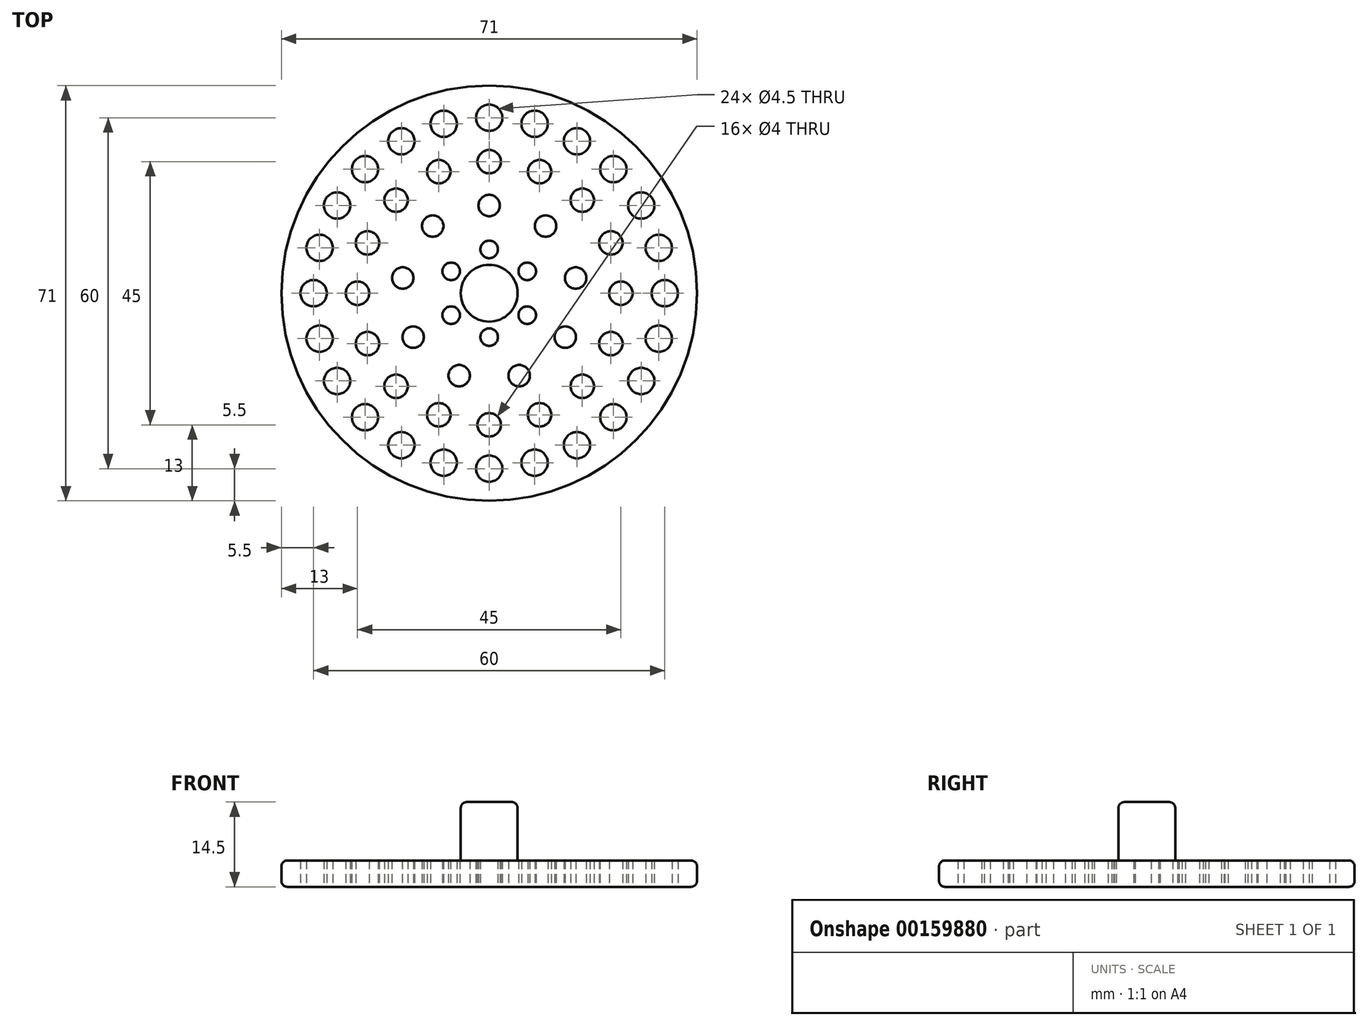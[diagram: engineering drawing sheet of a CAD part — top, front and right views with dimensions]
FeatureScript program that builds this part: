
annotation { "Feature Type Name" : "Feature", "Feature Type Description" : "" }
export const myFeature = defineFeature(function(context is Context, id is Id, definition is map)
    precondition{}
    {
        {
            var Q0;
            Q0=qCreatedBy(makeId("Top.planeOp"),FACE);
            var sketch = newSketch(context, id + "F0", { "sketchPlane" : qUnion([Q0])});
            skCircle(sketch, "E0", {"center": v(0, 0) * mm, "radius": 35.5 * mm});
            skSolve(sketch);
        }
        {
            var Q0;
            Q0=makeQuery(id+"F0.imprint","IMPRINT",FACE,{"disambiguationData":[TD([[makeQuery(id+"F0.imprint","IMPRINT",EDGE,{"derivedFrom":sQuery(id+"F0.wireOp",EDGE,"E0")}),1.0]])]});
            var sketch = newSketch(context, id + "F1", { "sketchPlane" : qUnion([Q0])});
            skCircle(sketch, "E1", {"center": v(0, 0) * mm, "radius": 7.5 * mm, "construction": true});
            skCircle(sketch, "E2", {"center": v(0, 7.5) * mm, "radius": 1.5 * mm});
            skCircle(sketch, "E3.1.1", {"center": v(-6.5, 3.75) * mm, "radius": 1.5 * mm});
            skCircle(sketch, "E3.2.1", {"center": v(-6.5, -3.75) * mm, "radius": 1.5 * mm});
            skCircle(sketch, "E3.3.1", {"center": v(0, -7.5) * mm, "radius": 1.5 * mm});
            skCircle(sketch, "E3.4.1", {"center": v(6.5, -3.75) * mm, "radius": 1.5 * mm});
            skCircle(sketch, "E3.5.1", {"center": v(6.5, 3.75) * mm, "radius": 1.5 * mm});
            skSolve(sketch);
        }
        {
            var Q0;
            Q0=makeQuery(id+"F0.imprint","IMPRINT",FACE,{"disambiguationData":[TD([[makeQuery(id+"F0.imprint","IMPRINT",EDGE,{"derivedFrom":sQuery(id+"F0.wireOp",EDGE,"E0")}),1.0]])]});
            var sketch = newSketch(context, id + "F2", { "sketchPlane" : qUnion([Q0])});
            skCircle(sketch, "E4", {"center": v(0, 0) * mm, "radius": 15 * mm, "construction": true});
            skCircle(sketch, "E5", {"center": v(0, 15) * mm, "radius": 1.83 * mm});
            skCircle(sketch, "E6.1.0", {"center": v(-9.64, 11.5) * mm, "radius": 1.83 * mm});
            skCircle(sketch, "E6.2.0", {"center": v(-14.77, 2.6) * mm, "radius": 1.83 * mm});
            skCircle(sketch, "E6.3.0", {"center": v(-13, -7.5) * mm, "radius": 1.83 * mm});
            skCircle(sketch, "E6.4.0", {"center": v(-5.13, -14.1) * mm, "radius": 1.83 * mm});
            skCircle(sketch, "E6.5.0", {"center": v(5.13, -14.1) * mm, "radius": 1.83 * mm});
            skCircle(sketch, "E6.6.0", {"center": v(13, -7.5) * mm, "radius": 1.83 * mm});
            skCircle(sketch, "E6.7.0", {"center": v(14.77, 2.6) * mm, "radius": 1.83 * mm});
            skCircle(sketch, "E6.8.0", {"center": v(9.64, 11.5) * mm, "radius": 1.83 * mm});
            skSolve(sketch);
        }
        {
            var Q0;
            Q0=makeQuery(id+"F0.imprint","IMPRINT",FACE,{"disambiguationData":[TD([[makeQuery(id+"F0.imprint","IMPRINT",EDGE,{"derivedFrom":sQuery(id+"F0.wireOp",EDGE,"E0")}),1.0]])]});
            var sketch = newSketch(context, id + "F3", { "sketchPlane" : qUnion([Q0])});
            skCircle(sketch, "E7", {"center": v(0, 0) * mm, "radius": 22.5 * mm, "construction": true});
            skCircle(sketch, "E8", {"center": v(0, 22.5) * mm, "radius": 2 * mm});
            skCircle(sketch, "E9.1.0", {"center": v(-8.61, 20.79) * mm, "radius": 2 * mm});
            skCircle(sketch, "E9.2.0", {"center": v(-15.9, 15.9) * mm, "radius": 2 * mm});
            skCircle(sketch, "E9.3.0", {"center": v(-20.79, 8.61) * mm, "radius": 2 * mm});
            skCircle(sketch, "E9.4.0", {"center": v(-22.5, 0) * mm, "radius": 2 * mm});
            skCircle(sketch, "E9.5.0", {"center": v(-20.79, -8.61) * mm, "radius": 2 * mm});
            skCircle(sketch, "E9.6.0", {"center": v(-15.9, -15.9) * mm, "radius": 2 * mm});
            skCircle(sketch, "E9.7.0", {"center": v(-8.61, -20.79) * mm, "radius": 2 * mm});
            skCircle(sketch, "E9.8.0", {"center": v(0, -22.5) * mm, "radius": 2 * mm});
            skCircle(sketch, "E9.9.0", {"center": v(8.61, -20.79) * mm, "radius": 2 * mm});
            skCircle(sketch, "E9.10.0", {"center": v(15.9, -15.9) * mm, "radius": 2 * mm});
            skCircle(sketch, "E9.11.0", {"center": v(20.79, -8.61) * mm, "radius": 2 * mm});
            skCircle(sketch, "E9.12.0", {"center": v(22.5, 0) * mm, "radius": 2 * mm});
            skCircle(sketch, "E9.13.0", {"center": v(20.79, 8.61) * mm, "radius": 2 * mm});
            skCircle(sketch, "E9.14.0", {"center": v(15.9, 15.9) * mm, "radius": 2 * mm});
            skCircle(sketch, "E9.15.0", {"center": v(8.61, 20.79) * mm, "radius": 2 * mm});
            skSolve(sketch);
        }
        {
            var Q0;
            Q0=makeQuery(id+"F0.imprint","IMPRINT",FACE,{"disambiguationData":[TD([[makeQuery(id+"F0.imprint","IMPRINT",EDGE,{"derivedFrom":sQuery(id+"F0.wireOp",EDGE,"E0")}),1.0]])]});
            var sketch = newSketch(context, id + "F4", { "sketchPlane" : qUnion([Q0])});
            skCircle(sketch, "E10", {"center": v(0, 0) * mm, "radius": 30 * mm, "construction": true});
            skCircle(sketch, "E11", {"center": v(0, 30) * mm, "radius": 2.25 * mm});
            skCircle(sketch, "E12.1.0", {"center": v(-7.76, 28.98) * mm, "radius": 2.25 * mm});
            skCircle(sketch, "E12.2.0", {"center": v(-15, 25.98) * mm, "radius": 2.25 * mm});
            skCircle(sketch, "E13.1.3.0", {"center": v(-21.21, 21.21) * mm, "radius": 2.25 * mm});
            skCircle(sketch, "E13.1.4.0", {"center": v(-25.98, 15) * mm, "radius": 2.25 * mm});
            skCircle(sketch, "E13.1.5.0", {"center": v(-28.98, 7.76) * mm, "radius": 2.25 * mm});
            skCircle(sketch, "E13.1.6.0", {"center": v(-30, 0) * mm, "radius": 2.25 * mm});
            skCircle(sketch, "E13.1.7.0", {"center": v(-28.98, -7.76) * mm, "radius": 2.25 * mm});
            skCircle(sketch, "E13.1.8.0", {"center": v(-25.98, -15) * mm, "radius": 2.25 * mm});
            skCircle(sketch, "E13.1.9.0", {"center": v(-21.21, -21.21) * mm, "radius": 2.25 * mm});
            skCircle(sketch, "E13.1.10.0", {"center": v(-15, -25.98) * mm, "radius": 2.25 * mm});
            skCircle(sketch, "E13.1.11.0", {"center": v(-7.76, -28.98) * mm, "radius": 2.25 * mm});
            skCircle(sketch, "E13.1.12.0", {"center": v(0, -30) * mm, "radius": 2.25 * mm});
            skCircle(sketch, "E13.1.13.0", {"center": v(7.76, -28.98) * mm, "radius": 2.25 * mm});
            skCircle(sketch, "E13.1.14.0", {"center": v(15, -25.98) * mm, "radius": 2.25 * mm});
            skCircle(sketch, "E13.1.15.0", {"center": v(21.21, -21.21) * mm, "radius": 2.25 * mm});
            skCircle(sketch, "E13.1.16.0", {"center": v(25.98, -15) * mm, "radius": 2.25 * mm});
            skCircle(sketch, "E13.1.17.0", {"center": v(28.98, -7.76) * mm, "radius": 2.25 * mm});
            skCircle(sketch, "E13.1.18.0", {"center": v(30, 0) * mm, "radius": 2.25 * mm});
            skCircle(sketch, "E13.1.19.0", {"center": v(28.98, 7.76) * mm, "radius": 2.25 * mm});
            skCircle(sketch, "E13.1.20.0", {"center": v(25.98, 15) * mm, "radius": 2.25 * mm});
            skCircle(sketch, "E13.1.21.0", {"center": v(21.21, 21.21) * mm, "radius": 2.25 * mm});
            skCircle(sketch, "E13.1.22.0", {"center": v(15, 25.98) * mm, "radius": 2.25 * mm});
            skCircle(sketch, "E13.1.23.0", {"center": v(7.76, 28.98) * mm, "radius": 2.25 * mm});
            skSolve(sketch);
        }
        {
            var Q0;
            Q0 = qSketchRegion(id + "F4", true);
            extrude(context, id + "F5", {"entities" : qUnion([Q0]), "depth" : 5 * mm});
        }
        {
            var Q0;
            Q0 = qSketchRegion(id + "F3", true);
            extrude(context, id + "F6", {"entities" : qUnion([Q0]), "depth" : 5 * mm});
        }
        {
            var Q0;
            Q0 = qSketchRegion(id + "F2", true);
            extrude(context, id + "F7", {"entities" : qUnion([Q0]), "depth" : 5 * mm});
        }
        {
            var Q0;
            Q0 = qSketchRegion(id + "F1", true);
            extrude(context, id + "F8", {"entities" : qUnion([Q0]), "depth" : 5 * mm});
        }
        {
            var Q0;
            Q0 = qSketchRegion(id + "F0", true);
            extrude(context, id + "F9", {"entities" : qUnion([Q0]), "depth" : 4.5 * mm});
        }
        {
            var Q0;
            Q0=makeQuery(id+"F5.opExtrude","SWEPT_BODY",BODY,{"disambiguationData":[OSD([sQuery(id+"F4.wireOp",EDGE,"E11")])]});
            var Q1;
            Q1=makeQuery(id+"F5.opExtrude","SWEPT_BODY",BODY,{"disambiguationData":[OSD([sQuery(id+"F4.wireOp",EDGE,"E13.1.3.0")])]});
            var Q2;
            Q2=makeQuery(id+"F5.opExtrude","SWEPT_BODY",BODY,{"disambiguationData":[OSD([sQuery(id+"F4.wireOp",EDGE,"E13.1.7.0")])]});
            var Q3;
            Q3=makeQuery(id+"F5.opExtrude","SWEPT_BODY",BODY,{"disambiguationData":[OSD([sQuery(id+"F4.wireOp",EDGE,"E12.1.0")])]});
            var Q4;
            Q4=makeQuery(id+"F5.opExtrude","SWEPT_BODY",BODY,{"disambiguationData":[OSD([sQuery(id+"F4.wireOp",EDGE,"E12.2.0")])]});
            var Q5;
            Q5=makeQuery(id+"F5.opExtrude","SWEPT_BODY",BODY,{"disambiguationData":[OSD([sQuery(id+"F4.wireOp",EDGE,"E13.1.4.0")])]});
            var Q6;
            Q6=makeQuery(id+"F5.opExtrude","SWEPT_BODY",BODY,{"disambiguationData":[OSD([sQuery(id+"F4.wireOp",EDGE,"E13.1.5.0")])]});
            var Q7;
            Q7=makeQuery(id+"F5.opExtrude","SWEPT_BODY",BODY,{"disambiguationData":[OSD([sQuery(id+"F4.wireOp",EDGE,"E13.1.6.0")])]});
            var Q8;
            Q8=makeQuery(id+"F5.opExtrude","SWEPT_BODY",BODY,{"disambiguationData":[OSD([sQuery(id+"F4.wireOp",EDGE,"E13.1.8.0")])]});
            var Q9;
            Q9=makeQuery(id+"F5.opExtrude","SWEPT_BODY",BODY,{"disambiguationData":[OSD([sQuery(id+"F4.wireOp",EDGE,"E13.1.9.0")])]});
            var Q10;
            Q10=makeQuery(id+"F5.opExtrude","SWEPT_BODY",BODY,{"disambiguationData":[OSD([sQuery(id+"F4.wireOp",EDGE,"E13.1.10.0")])]});
            var Q11;
            Q11=makeQuery(id+"F5.opExtrude","SWEPT_BODY",BODY,{"disambiguationData":[OSD([sQuery(id+"F4.wireOp",EDGE,"E13.1.11.0")])]});
            var Q12;
            Q12=makeQuery(id+"F5.opExtrude","SWEPT_BODY",BODY,{"disambiguationData":[OSD([sQuery(id+"F4.wireOp",EDGE,"E13.1.12.0")])]});
            var Q13;
            Q13=makeQuery(id+"F5.opExtrude","SWEPT_BODY",BODY,{"disambiguationData":[OSD([sQuery(id+"F4.wireOp",EDGE,"E13.1.13.0")])]});
            var Q14;
            Q14=makeQuery(id+"F5.opExtrude","SWEPT_BODY",BODY,{"disambiguationData":[OSD([sQuery(id+"F4.wireOp",EDGE,"E13.1.14.0")])]});
            var Q15;
            Q15=makeQuery(id+"F5.opExtrude","SWEPT_BODY",BODY,{"disambiguationData":[OSD([sQuery(id+"F4.wireOp",EDGE,"E13.1.15.0")])]});
            var Q16;
            Q16=makeQuery(id+"F5.opExtrude","SWEPT_BODY",BODY,{"disambiguationData":[OSD([sQuery(id+"F4.wireOp",EDGE,"E13.1.16.0")])]});
            var Q17;
            Q17=makeQuery(id+"F5.opExtrude","SWEPT_BODY",BODY,{"disambiguationData":[OSD([sQuery(id+"F4.wireOp",EDGE,"E13.1.17.0")])]});
            var Q18;
            Q18=makeQuery(id+"F5.opExtrude","SWEPT_BODY",BODY,{"disambiguationData":[OSD([sQuery(id+"F4.wireOp",EDGE,"E13.1.18.0")])]});
            var Q19;
            Q19=makeQuery(id+"F5.opExtrude","SWEPT_BODY",BODY,{"disambiguationData":[OSD([sQuery(id+"F4.wireOp",EDGE,"E13.1.19.0")])]});
            var Q20;
            Q20=makeQuery(id+"F5.opExtrude","SWEPT_BODY",BODY,{"disambiguationData":[OSD([sQuery(id+"F4.wireOp",EDGE,"E13.1.20.0")])]});
            var Q21;
            Q21=makeQuery(id+"F5.opExtrude","SWEPT_BODY",BODY,{"disambiguationData":[OSD([sQuery(id+"F4.wireOp",EDGE,"E13.1.21.0")])]});
            var Q22;
            Q22=makeQuery(id+"F5.opExtrude","SWEPT_BODY",BODY,{"disambiguationData":[OSD([sQuery(id+"F4.wireOp",EDGE,"E13.1.22.0")])]});
            var Q23;
            Q23=makeQuery(id+"F5.opExtrude","SWEPT_BODY",BODY,{"disambiguationData":[OSD([sQuery(id+"F4.wireOp",EDGE,"E13.1.23.0")])]});
            var Q24;
            Q24=makeQuery(id+"F6.opExtrude","SWEPT_BODY",BODY,{"disambiguationData":[OSD([sQuery(id+"F3.wireOp",EDGE,"E9.15.0")])]});
            var Q25;
            Q25=makeQuery(id+"F6.opExtrude","SWEPT_BODY",BODY,{"disambiguationData":[OSD([sQuery(id+"F3.wireOp",EDGE,"E8")])]});
            var Q26;
            Q26=makeQuery(id+"F6.opExtrude","SWEPT_BODY",BODY,{"disambiguationData":[OSD([sQuery(id+"F3.wireOp",EDGE,"E9.1.0")])]});
            var Q27;
            Q27=makeQuery(id+"F6.opExtrude","SWEPT_BODY",BODY,{"disambiguationData":[OSD([sQuery(id+"F3.wireOp",EDGE,"E9.2.0")])]});
            var Q28;
            Q28=makeQuery(id+"F6.opExtrude","SWEPT_BODY",BODY,{"disambiguationData":[OSD([sQuery(id+"F3.wireOp",EDGE,"E9.3.0")])]});
            var Q29;
            Q29=makeQuery(id+"F6.opExtrude","SWEPT_BODY",BODY,{"disambiguationData":[OSD([sQuery(id+"F3.wireOp",EDGE,"E9.4.0")])]});
            var Q30;
            Q30=makeQuery(id+"F6.opExtrude","SWEPT_BODY",BODY,{"disambiguationData":[OSD([sQuery(id+"F3.wireOp",EDGE,"E9.5.0")])]});
            var Q31;
            Q31=makeQuery(id+"F6.opExtrude","SWEPT_BODY",BODY,{"disambiguationData":[OSD([sQuery(id+"F3.wireOp",EDGE,"E9.6.0")])]});
            var Q32;
            Q32=makeQuery(id+"F6.opExtrude","SWEPT_BODY",BODY,{"disambiguationData":[OSD([sQuery(id+"F3.wireOp",EDGE,"E9.7.0")])]});
            var Q33;
            Q33=makeQuery(id+"F6.opExtrude","SWEPT_BODY",BODY,{"disambiguationData":[OSD([sQuery(id+"F3.wireOp",EDGE,"E9.8.0")])]});
            var Q34;
            Q34=makeQuery(id+"F6.opExtrude","SWEPT_BODY",BODY,{"disambiguationData":[OSD([sQuery(id+"F3.wireOp",EDGE,"E9.9.0")])]});
            var Q35;
            Q35=makeQuery(id+"F6.opExtrude","SWEPT_BODY",BODY,{"disambiguationData":[OSD([sQuery(id+"F3.wireOp",EDGE,"E9.10.0")])]});
            var Q36;
            Q36=makeQuery(id+"F6.opExtrude","SWEPT_BODY",BODY,{"disambiguationData":[OSD([sQuery(id+"F3.wireOp",EDGE,"E9.11.0")])]});
            var Q37;
            Q37=makeQuery(id+"F6.opExtrude","SWEPT_BODY",BODY,{"disambiguationData":[OSD([sQuery(id+"F3.wireOp",EDGE,"E9.12.0")])]});
            var Q38;
            Q38=makeQuery(id+"F6.opExtrude","SWEPT_BODY",BODY,{"disambiguationData":[OSD([sQuery(id+"F3.wireOp",EDGE,"E9.13.0")])]});
            var Q39;
            Q39=makeQuery(id+"F6.opExtrude","SWEPT_BODY",BODY,{"disambiguationData":[OSD([sQuery(id+"F3.wireOp",EDGE,"E9.14.0")])]});
            var Q40;
            Q40=makeQuery(id+"F7.opExtrude","SWEPT_BODY",BODY,{"disambiguationData":[OSD([sQuery(id+"F2.wireOp",EDGE,"E6.8.0")])]});
            var Q41;
            Q41=makeQuery(id+"F7.opExtrude","SWEPT_BODY",BODY,{"disambiguationData":[OSD([sQuery(id+"F2.wireOp",EDGE,"E6.7.0")])]});
            var Q42;
            Q42=makeQuery(id+"F7.opExtrude","SWEPT_BODY",BODY,{"disambiguationData":[OSD([sQuery(id+"F2.wireOp",EDGE,"E6.6.0")])]});
            var Q43;
            Q43=makeQuery(id+"F7.opExtrude","SWEPT_BODY",BODY,{"disambiguationData":[OSD([sQuery(id+"F2.wireOp",EDGE,"E6.5.0")])]});
            var Q44;
            Q44=makeQuery(id+"F7.opExtrude","SWEPT_BODY",BODY,{"disambiguationData":[OSD([sQuery(id+"F2.wireOp",EDGE,"E6.4.0")])]});
            var Q45;
            Q45=makeQuery(id+"F7.opExtrude","SWEPT_BODY",BODY,{"disambiguationData":[OSD([sQuery(id+"F2.wireOp",EDGE,"E6.3.0")])]});
            var Q46;
            Q46=makeQuery(id+"F7.opExtrude","SWEPT_BODY",BODY,{"disambiguationData":[OSD([sQuery(id+"F2.wireOp",EDGE,"E6.2.0")])]});
            var Q47;
            Q47=makeQuery(id+"F7.opExtrude","SWEPT_BODY",BODY,{"disambiguationData":[OSD([sQuery(id+"F2.wireOp",EDGE,"E6.1.0")])]});
            var Q48;
            Q48=makeQuery(id+"F7.opExtrude","SWEPT_BODY",BODY,{"disambiguationData":[OSD([sQuery(id+"F2.wireOp",EDGE,"E5")])]});
            var Q49;
            Q49=makeQuery(id+"F8.opExtrude","SWEPT_BODY",BODY,{"disambiguationData":[OSD([sQuery(id+"F1.wireOp",EDGE,"E2")])]});
            var Q50;
            Q50=makeQuery(id+"F8.opExtrude","SWEPT_BODY",BODY,{"disambiguationData":[OSD([sQuery(id+"F1.wireOp",EDGE,"E3.5.1")])]});
            var Q51;
            Q51=makeQuery(id+"F8.opExtrude","SWEPT_BODY",BODY,{"disambiguationData":[OSD([sQuery(id+"F1.wireOp",EDGE,"E3.4.1")])]});
            var Q52;
            Q52=makeQuery(id+"F8.opExtrude","SWEPT_BODY",BODY,{"disambiguationData":[OSD([sQuery(id+"F1.wireOp",EDGE,"E3.3.1")])]});
            var Q53;
            Q53=makeQuery(id+"F8.opExtrude","SWEPT_BODY",BODY,{"disambiguationData":[OSD([sQuery(id+"F1.wireOp",EDGE,"E3.2.1")])]});
            var Q54;
            Q54=makeQuery(id+"F8.opExtrude","SWEPT_BODY",BODY,{"disambiguationData":[OSD([sQuery(id+"F1.wireOp",EDGE,"E3.1.1")])]});
            var Q55;
            Q55=makeQuery(id+"F9.opExtrude","SWEPT_BODY",BODY,{"disambiguationData":[OSD([sQuery(id+"F0.wireOp",EDGE,"E0")])]});
            booleanBodies(context, id + "F10", {"operationType" : BooleanOperationType.SUBTRACTION, "tools" : qUnion([Q0, Q1, Q2, Q3, Q4, Q5, Q6, Q7, Q8, Q9, Q10, Q11, Q12, Q13, Q14, Q15, Q16, Q17, Q18, Q19, Q20, Q21, Q22, Q23, Q24, Q25, Q26, Q27, Q28, Q29, Q30, Q31, Q32, Q33, Q34, Q35, Q36, Q37, Q38, Q39, Q40, Q41, Q42, Q43, Q44, Q45, Q46, Q47, Q48, Q49, Q50, Q51, Q52, Q53, Q54]), "targets" : qUnion([Q55])});
        }
        {
            var Q0;
            Q0=makeQuery(id+"F9.opExtrude","CAP_EDGE",EDGE,{"disambiguationData":[OSD([sQuery(id+"F0.wireOp",EDGE,"E0")])],"isStart":true});
            var Q1;
            Q1=makeQuery(id+"F9.opExtrude","CAP_EDGE",EDGE,{"disambiguationData":[OSD([sQuery(id+"F0.wireOp",EDGE,"E0")])],"isStart":false});
            fillet(context, id + "F11", {"entities" : qUnion([Q0, Q1]), "radius" : 1 * mm, "tangentPropagation" : true, "allowEdgeOverflow" : false});
        }
        {
            var Q0;
            Q0=makeQuery(id+"F9.opExtrude","CAP_FACE",FACE,{"disambiguationData":[OSD([sQuery(id+"F0.wireOp",EDGE,"E0")])],"isStart":false});
            var sketch = newSketch(context, id + "F12", { "sketchPlane" : qUnion([Q0])});
            skCircle(sketch, "E14", {"center": v(0, 0) * mm, "radius": 4.85 * mm});
            skSolve(sketch);
        }
        {
            var Q0;
            Q0=makeQuery(id+"F12.imprint","IMPRINT",FACE,{"disambiguationData":[TD([[makeQuery(id+"F12.imprint","IMPRINT",EDGE,{"derivedFrom":sQuery(id+"F12.wireOp",EDGE,"E14")}),1.0]])]});
            extrude(context, id + "F13", {"entities" : qUnion([Q0]), "operationType" : NewBodyOperationType.ADD, "depth" : 10 * mm});
        }
        {
            var Q0;
            Q0=makeQuery(id+"F13.opExtrude","CAP_EDGE",EDGE,{"disambiguationData":[OSD([sQuery(id+"F12.wireOp",EDGE,"E14")])],"isStart":false});
            fillet(context, id + "F14", {"entities" : qUnion([Q0]), "radius" : 1 * mm, "tangentPropagation" : true, "allowEdgeOverflow" : false});
        }
    });
